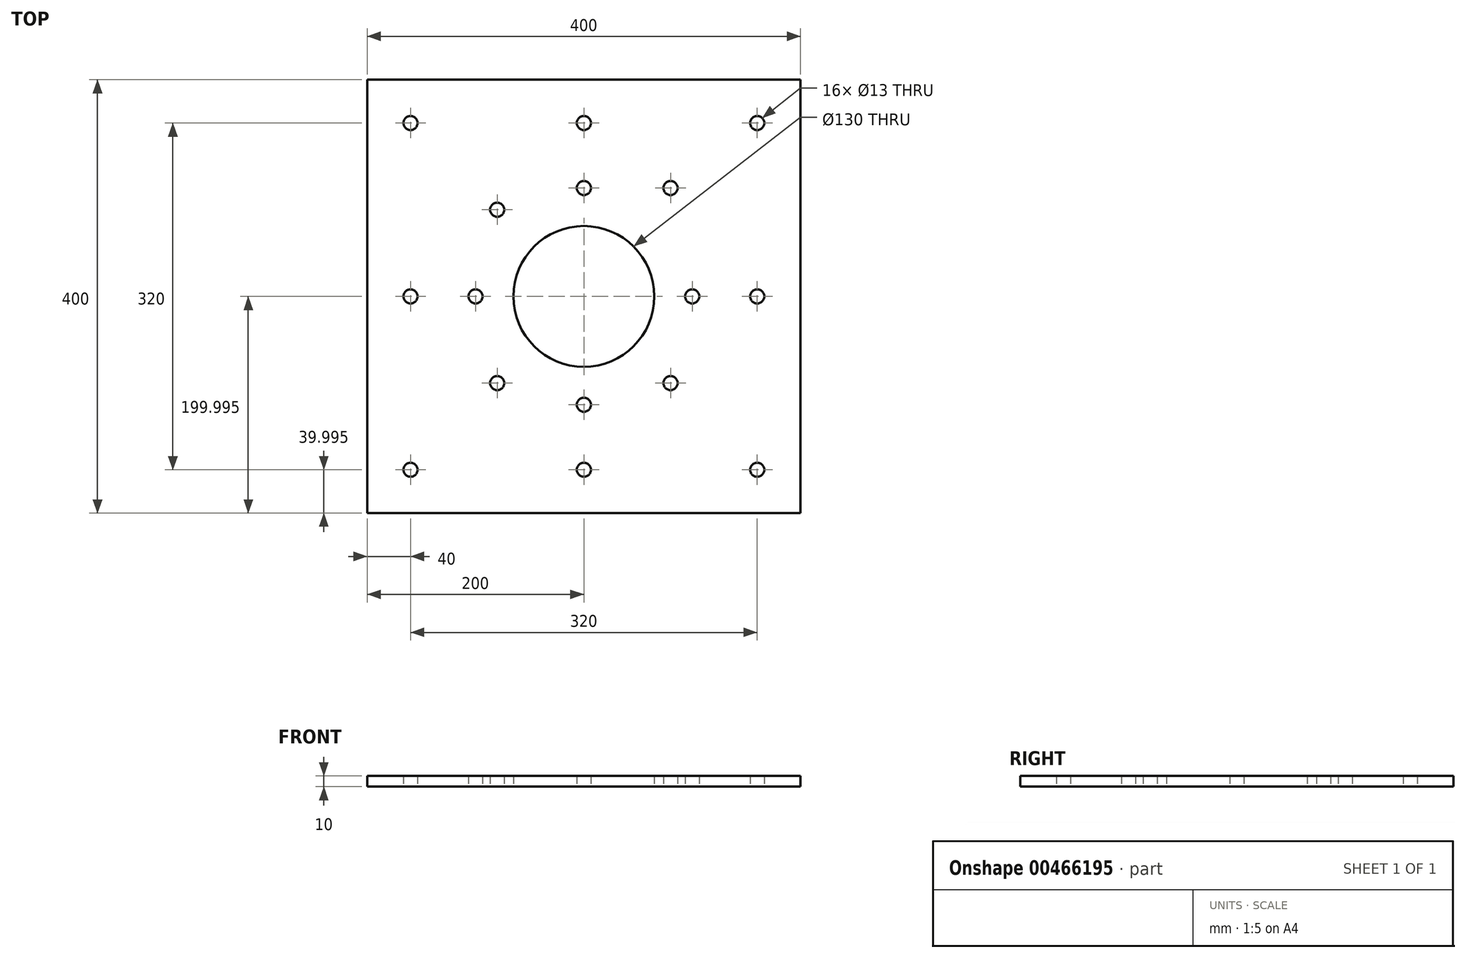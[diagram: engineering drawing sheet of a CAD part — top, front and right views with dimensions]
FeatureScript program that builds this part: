
annotation { "Feature Type Name" : "Feature", "Feature Type Description" : "" }
export const myFeature = defineFeature(function(context is Context, id is Id, definition is map)
    precondition{}
    {
        {
            var Q0;
            Q0=qCreatedBy(makeId("Top.planeOp"),FACE);
            var sketch = newSketch(context, id + "F0", { "sketchPlane" : qUnion([Q0])});
            skLineSegment(sketch, "E0.bottom", {"start": v(-200, -161.38) * mm, "end": v(200, -161.38) * mm});
            skLineSegment(sketch, "E0.top", {"start": v(-200, 238.62) * mm, "end": v(200, 238.62) * mm});
            skLineSegment(sketch, "E0.left", {"start": v(-200, -161.38) * mm, "end": v(-200, 238.62) * mm});
            skLineSegment(sketch, "E0.right", {"start": v(200, -161.38) * mm, "end": v(200, 238.62) * mm});
            skCircle(sketch, "E1", {"center": v(-160, 198.62) * mm, "radius": 6.5 * mm});
            skCircle(sketch, "E2", {"center": v(160, 198.62) * mm, "radius": 6.5 * mm});
            skCircle(sketch, "E3", {"center": v(80, 138.62) * mm, "radius": 6.5 * mm});
            skCircle(sketch, "E4", {"center": v(0, 38.62) * mm, "radius": 65 * mm});
            skCircle(sketch, "E5", {"center": v(80, -41.38) * mm, "radius": 6.5 * mm});
            skCircle(sketch, "E6", {"center": v(-80, 118.62) * mm, "radius": 6.5 * mm});
            skCircle(sketch, "E7", {"center": v(-80, -41.38) * mm, "radius": 6.5 * mm});
            skCircle(sketch, "E8", {"center": v(-160, -121.38) * mm, "radius": 6.5 * mm});
            skCircle(sketch, "E9", {"center": v(0, 198.62) * mm, "radius": 6.5 * mm});
            skCircle(sketch, "E10", {"center": v(0, 138.62) * mm, "radius": 6.5 * mm});
            skCircle(sketch, "E11", {"center": v(160, 38.62) * mm, "radius": 6.5 * mm});
            skCircle(sketch, "E12", {"center": v(100, 38.62) * mm, "radius": 6.5 * mm});
            skCircle(sketch, "E13", {"center": v(-160, 38.62) * mm, "radius": 6.5 * mm});
            skPoint(sketch, "E13.centerSnap0", {"position": v(-200, 38.62) * mm});
            skCircle(sketch, "E14", {"center": v(-100, 38.62) * mm, "radius": 6.5 * mm});
            skCircle(sketch, "E15", {"center": v(0, -61.38) * mm, "radius": 6.5 * mm});
            skCircle(sketch, "E16", {"center": v(0, -121.38) * mm, "radius": 6.5 * mm});
            skCircle(sketch, "E17", {"center": v(160, -121.38) * mm, "radius": 6.5 * mm});
            skSolve(sketch);
        }
        {
            var Q0;
            Q0 = qSketchRegion(id + "F0", true);
            extrude(context, id + "F1", {"entities" : qUnion([Q0]), "depth" : 10 * mm});
        }
    });
